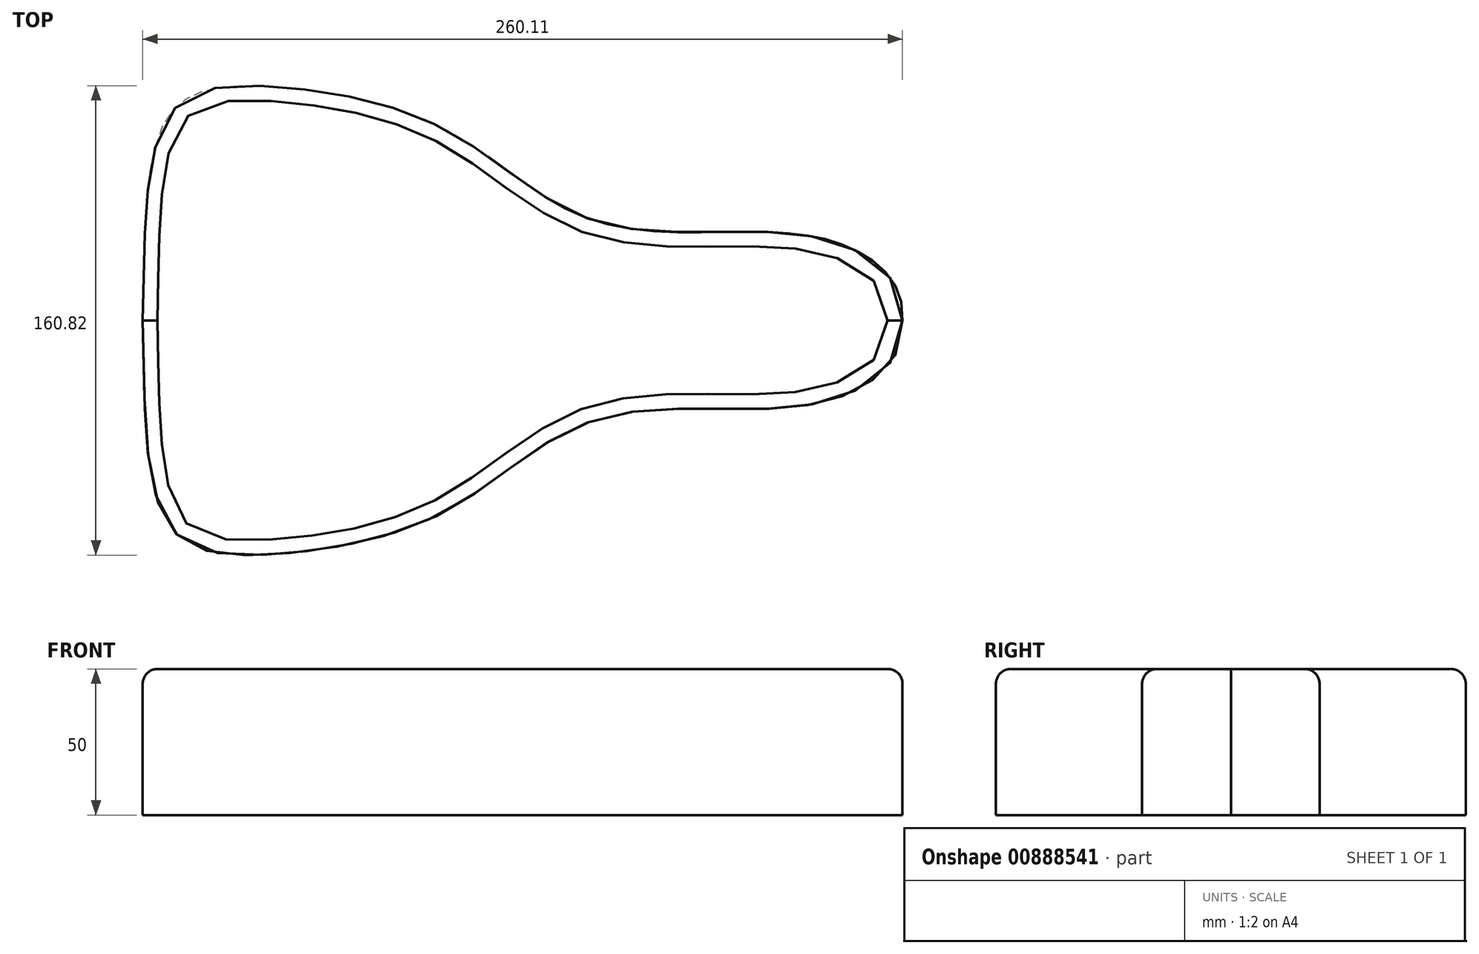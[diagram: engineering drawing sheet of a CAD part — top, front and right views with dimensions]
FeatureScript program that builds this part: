
annotation { "Feature Type Name" : "Feature", "Feature Type Description" : "" }
export const myFeature = defineFeature(function(context is Context, id is Id, definition is map)
    precondition{}
    {
        {
            var Q0;
            Q0=qCreatedBy(makeId("Top.planeOp"),FACE);
            var sketch = newSketch(context, id + "F0", { "sketchPlane" : qUnion([Q0])});
            skLineSegment(sketch, "E0", {"start": v(0, 0) * mm, "end": v(260, 0) * mm});
            skFitSpline(sketch, "E1", {"points": [v(0, 0) * mm, v(10.12, -71.66) * mm, v(45.56, -80) * mm, v(103.7, -65.36) * mm, v(152.15, -35) * mm, v(208.3, -30.37) * mm, v(244.48, -23.76) * mm, v(260, 0) * mm], "startDerivative": vector(15.8, -505.37) * mm, "endDerivative": vector(-30.64, 314.77) * mm});
            skFitSpline(sketch, "E2.MirrorCS", {"points": [v(0, 0) * mm, v(10.12, 71.66) * mm, v(45.56, 80) * mm, v(103.7, 65.36) * mm, v(152.15, 35) * mm, v(208.3, 30.37) * mm, v(244.48, 23.76) * mm, v(260, 0) * mm], "startDerivative": vector(15.8, 505.37) * mm, "endDerivative": vector(-30.64, -314.77) * mm});
            skSolve(sketch);
        }
        {
            var Q0;
            Q0 = qSketchRegion(id + "F0", true);
            var Q1;
            Q1=makeQuery(id+"F0.imprint","IMPRINT",FACE,{"disambiguationData":[TD([[makeQuery(id+"F0.imprint","IMPRINT",EDGE,{"derivedFrom":sQuery(id+"F0.wireOp",EDGE,"E0")}),-1.0]])]});
            extrude(context, id + "F1", {"entities" : qUnion([Q0, Q1]), "depth" : 50 * mm, "offsetDistance" : 25 * mm});
        }
        {
            var Q0;
            Q0=makeQuery(id+"F1.opExtrude","CAP_FACE",FACE,{"disambiguationData":[OSD([sQuery(id+"F0.wireOp",EDGE,"E1"),sQuery(id+"F0.wireOp",EDGE,"E2.MirrorCS")])],"isStart":false});
            fillet(context, id + "F2", {"entities" : qUnion([Q0]), "radius" : 5 * mm, "tangentPropagation" : true, "allowEdgeOverflow" : false});
        }
    });
